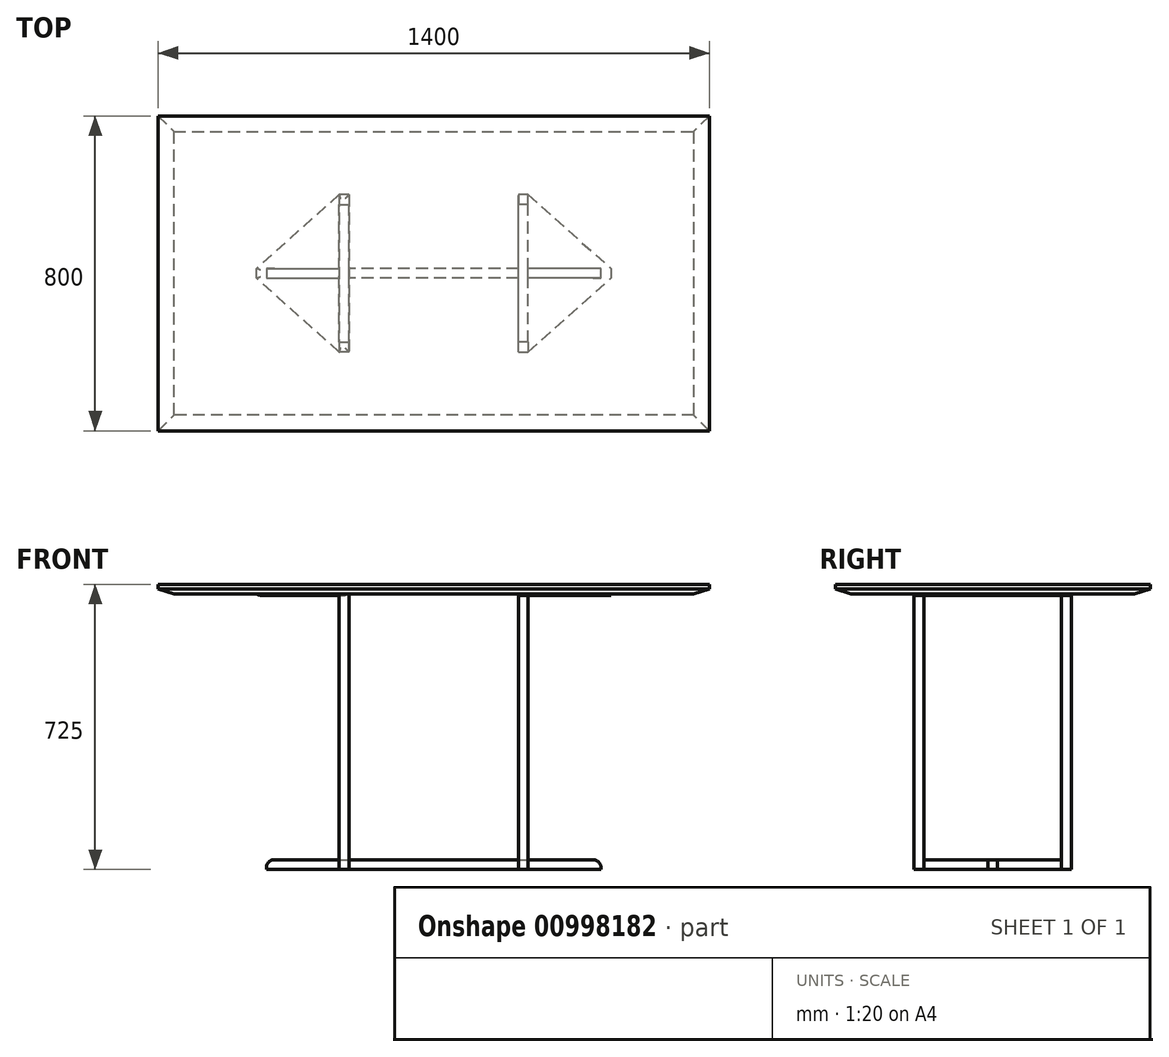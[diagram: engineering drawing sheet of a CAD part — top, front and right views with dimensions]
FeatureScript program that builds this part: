
annotation { "Feature Type Name" : "Feature", "Feature Type Description" : "" }
export const myFeature = defineFeature(function(context is Context, id is Id, definition is map)
    precondition{}
    {
        {
            var Q0;
            Q0=qCreatedBy(makeId("Top.planeOp"),FACE);
            var sketch = newSketch(context, id + "F0", { "sketchPlane" : qUnion([Q0])});
            skLineSegment(sketch, "E0.bottom", {"start": v(0, 0) * mm, "end": v(-1400, 0) * mm, "construction": true});
            skLineSegment(sketch, "E0.top", {"start": v(0, 800) * mm, "end": v(-1400, 800) * mm, "construction": true});
            skLineSegment(sketch, "E0.left", {"start": v(0, 0) * mm, "end": v(0, 800) * mm, "construction": true});
            skLineSegment(sketch, "E0.right", {"start": v(-1400, 0) * mm, "end": v(-1400, 800) * mm, "construction": true});
            skLineSegment(sketch, "E1", {"start": v(-700, 0) * mm, "end": v(-700, 800) * mm, "construction": true});
            skLineSegment(sketch, "E2", {"start": v(-1400, 400) * mm, "end": v(0, 400) * mm, "construction": true});
            skLineSegment(sketch, "E3", {"start": v(0, 400) * mm, "end": v(-250, 400) * mm, "construction": true});
            skLineSegment(sketch, "E4", {"start": v(0, 400) * mm, "end": v(-460, 400) * mm, "construction": true});
            skLineSegment(sketch, "E5", {"start": v(-460, 400) * mm, "end": v(-460, 800) * mm, "construction": true});
            skLineSegment(sketch, "E6", {"start": v(-460, 800) * mm, "end": v(-460, 600) * mm, "construction": true});
            skLineSegment(sketch, "E7", {"start": v(-460, 600) * mm, "end": v(-485, 600) * mm});
            skLineSegment(sketch, "E8", {"start": v(-485, 600) * mm, "end": v(-485, 575) * mm});
            skLineSegment(sketch, "E9", {"start": v(-485, 575) * mm, "end": v(-460, 575) * mm});
            skLineSegment(sketch, "E10", {"start": v(-460, 575) * mm, "end": v(-460, 600) * mm});
            skLineSegment(sketch, "E11.MirrorCS", {"start": v(-460, 200) * mm, "end": v(-485, 200) * mm});
            skLineSegment(sketch, "E12.MirrorCS", {"start": v(-485, 225) * mm, "end": v(-460, 225) * mm});
            skLineSegment(sketch, "E13.MirrorCS", {"start": v(-485, 200) * mm, "end": v(-485, 225) * mm});
            skLineSegment(sketch, "E14.MirrorCS", {"start": v(-460, 225) * mm, "end": v(-460, 200) * mm});
            skLineSegment(sketch, "E15.MirrorCS", {"start": v(-940, 600) * mm, "end": v(-915, 600) * mm});
            skLineSegment(sketch, "E16.MirrorCS", {"start": v(-915, 600) * mm, "end": v(-915, 575) * mm});
            skLineSegment(sketch, "E17.MirrorCS", {"start": v(-915, 575) * mm, "end": v(-940, 575) * mm});
            skLineSegment(sketch, "E18.MirrorCS", {"start": v(-915, 200) * mm, "end": v(-915, 225) * mm});
            skLineSegment(sketch, "E19.MirrorCS", {"start": v(-915, 225) * mm, "end": v(-940, 225) * mm});
            skLineSegment(sketch, "E20.MirrorCS", {"start": v(-940, 200) * mm, "end": v(-915, 200) * mm});
            skLineSegment(sketch, "E21.MirrorCS", {"start": v(-940, 225) * mm, "end": v(-940, 200) * mm});
            skLineSegment(sketch, "E22", {"start": v(-940, 600) * mm, "end": v(-940, 575) * mm});
            skSolve(sketch);
        }
        {
            var Q0;
            Q0=qSketchRegion(id+"F0",true);
            extrude(context, id + "F1", {"entities" : qUnion([Q0]), "depth" : 700 * mm, "offsetDistance" : 25 * mm});
        }
        {
            var Q0;
            Q0=makeQuery(id+"F1.opExtrude","SWEPT_FACE",FACE,{"disambiguationData":[OSD([sQuery(id+"F0.wireOp",EDGE,"E9")])]});
            cPlane(context, id + "F2", {"entities" : qUnion([Q0]), "cplaneType" : CPlaneType.OFFSET, "offset" : 0 * mm, "width" : 150 * mm, "height" : 150 * mm});
        }
        {
            var Q0;
            Q0=qCreatedBy(id+"F2.planeOp",FACE);
            var sketch = newSketch(context, id + "F3", { "sketchPlane" : qUnion([Q0])});
            skLineSegment(sketch, "E23", {"start": v(0, 0) * mm, "end": v(-460, 0) * mm});
            skLineSegment(sketch, "E24", {"start": v(-460, 0) * mm, "end": v(-485, 0) * mm});
            skLineSegment(sketch, "E25", {"start": v(-485, 0) * mm, "end": v(-485, 25) * mm});
            skLineSegment(sketch, "E26", {"start": v(-485, 25) * mm, "end": v(-460, 25) * mm});
            skLineSegment(sketch, "E27", {"start": v(-460, 25) * mm, "end": v(-460, 0) * mm});
            skSolve(sketch);
        }
        {
            var Q0;
            Q0=qSketchRegion(id+"F3",true);
            extrude(context, id + "F4", {"entities" : qUnion([Q0]), "depth" : 350 * mm, "offsetDistance" : 25 * mm});
        }
        {
            var Q0;
            Q0=makeQuery(id+"F4.opExtrude","SWEPT_FACE",FACE,{"disambiguationData":[OSD([sQuery(id+"F3.wireOp",EDGE,"E27")])]});
            cPlane(context, id + "F5", {"entities" : qUnion([Q0]), "cplaneType" : CPlaneType.OFFSET, "offset" : 0 * mm, "width" : 150 * mm, "height" : 150 * mm});
        }
        {
            var Q0;
            Q0=qCreatedBy(id+"F5.planeOp",FACE);
            var sketch = newSketch(context, id + "F6", { "sketchPlane" : qUnion([Q0])});
            skLineSegment(sketch, "E28", {"start": v(0, 0) * mm, "end": v(387.5, 0) * mm, "construction": true});
            skLineSegment(sketch, "E29", {"start": v(387.5, 0) * mm, "end": v(412.5, 0) * mm});
            skLineSegment(sketch, "E30", {"start": v(412.5, 0) * mm, "end": v(412.5, 25) * mm});
            skLineSegment(sketch, "E31", {"start": v(412.5, 25) * mm, "end": v(387.5, 25) * mm});
            skLineSegment(sketch, "E32", {"start": v(387.5, 25) * mm, "end": v(387.5, 0) * mm});
            skSolve(sketch);
        }
        {
            var Q0;
            Q0=qSketchRegion(id+"F6",true);
            extrude(context, id + "F7", {"entities" : qUnion([Q0]), "depth" : 185 * mm, "offsetDistance" : 25 * mm});
        }
        {
            var Q0;
            Q0=makeQuery(id+"F1.opExtrude","SWEPT_FACE",FACE,{"disambiguationData":[OSD([sQuery(id+"F0.wireOp",EDGE,"E17.MirrorCS")])]});
            cPlane(context, id + "F8", {"entities" : qUnion([Q0]), "cplaneType" : CPlaneType.OFFSET, "offset" : 0 * mm, "width" : 150 * mm, "height" : 150 * mm});
        }
        {
            var Q0;
            Q0=qCreatedBy(id+"F8.planeOp",FACE);
            var sketch = newSketch(context, id + "F9", { "sketchPlane" : qUnion([Q0])});
            skLineSegment(sketch, "E33", {"start": v(0, 0) * mm, "end": v(-700, 0) * mm, "construction": true});
            skLineSegment(sketch, "E34", {"start": v(-700, 0) * mm, "end": v(-915, 0) * mm, "construction": true});
            skLineSegment(sketch, "E35", {"start": v(-915, 0) * mm, "end": v(-940, 0) * mm});
            skLineSegment(sketch, "E36", {"start": v(-940, 0) * mm, "end": v(-940, 25) * mm});
            skLineSegment(sketch, "E37", {"start": v(-940, 25) * mm, "end": v(-915, 25) * mm});
            skLineSegment(sketch, "E38", {"start": v(-915, 25) * mm, "end": v(-915, 0) * mm});
            skSolve(sketch);
        }
        {
            var Q0;
            Q0=qSketchRegion(id+"F9",true);
            extrude(context, id + "F10", {"entities" : qUnion([Q0]), "operationType" : NewBodyOperationType.ADD, "depth" : 350 * mm, "offsetDistance" : 25 * mm});
        }
        {
            var Q0;
            Q0=makeQuery(id+"F10.boolean.opBoolean","MERGE",FACE,{"derivedFrom":[makeQuery(id+"F1.opExtrude","SWEPT_FACE",FACE,{"disambiguationData":[OSD([sQuery(id+"F0.wireOp",EDGE,"E22")])]}),makeQuery(id+"F10.opExtrude","SWEPT_FACE",FACE,{"disambiguationData":[OSD([sQuery(id+"F9.wireOp",EDGE,"E36")])]})]});
            cPlane(context, id + "F11", {"entities" : qUnion([Q0]), "cplaneType" : CPlaneType.OFFSET, "offset" : 0 * mm, "width" : 150 * mm, "height" : 150 * mm});
        }
        {
            var Q0;
            Q0=qCreatedBy(id+"F11.planeOp",FACE);
            var sketch = newSketch(context, id + "F12", { "sketchPlane" : qUnion([Q0])});
            skLineSegment(sketch, "E39", {"start": v(0, 0) * mm, "end": v(-387.5, 0) * mm, "construction": true});
            skLineSegment(sketch, "E40", {"start": v(-387.5, 0) * mm, "end": v(-387.5, 25) * mm});
            skLineSegment(sketch, "E41", {"start": v(-387.5, 25) * mm, "end": v(-412.5, 25) * mm});
            skLineSegment(sketch, "E42", {"start": v(-412.5, 25) * mm, "end": v(-412.5, 0) * mm});
            skLineSegment(sketch, "E43", {"start": v(-412.5, 0) * mm, "end": v(-387.5, 0) * mm});
            skSolve(sketch);
        }
        {
            var Q0;
            Q0=qSketchRegion(id+"F12",true);
            extrude(context, id + "F13", {"entities" : qUnion([Q0]), "depth" : 185 * mm, "offsetDistance" : 25 * mm});
        }
        {
            var Q0;
            Q0=makeQuery(id+"F1.opExtrude","CAP_FACE",FACE,{"disambiguationData":[OSD([sQuery(id+"F0.wireOp",EDGE,"E7"),sQuery(id+"F0.wireOp",EDGE,"E8"),sQuery(id+"F0.wireOp",EDGE,"E9"),sQuery(id+"F0.wireOp",EDGE,"E10")])],"isStart":false});
            cPlane(context, id + "F14", {"entities" : qUnion([Q0]), "cplaneType" : CPlaneType.OFFSET, "offset" : 0 * mm, "width" : 150 * mm, "height" : 150 * mm});
        }
        {
            var Q0;
            Q0=qCreatedBy(id+"F14.planeOp",FACE);
            var sketch = newSketch(context, id + "F15", { "sketchPlane" : qUnion([Q0])});
            skLineSegment(sketch, "E44.bottom", {"start": v(0, 0) * mm, "end": v(-1400, 0) * mm, "construction": true});
            skLineSegment(sketch, "E44.top", {"start": v(0, 800) * mm, "end": v(-1400, 800) * mm, "construction": true});
            skLineSegment(sketch, "E44.left", {"start": v(0, 0) * mm, "end": v(0, 800) * mm, "construction": true});
            skLineSegment(sketch, "E44.right", {"start": v(-1400, 0) * mm, "end": v(-1400, 800) * mm, "construction": true});
            skLineSegment(sketch, "E45", {"start": v(-700, 0) * mm, "end": v(-700, 400) * mm, "construction": true});
            skLineSegment(sketch, "E46", {"start": v(0, 400) * mm, "end": v(-250, 400) * mm, "construction": true});
            skLineSegment(sketch, "E47", {"start": v(-250, 400) * mm, "end": v(-250, 412.5) * mm});
            skLineSegment(sketch, "E48", {"start": v(-700, 400) * mm, "end": v(-485, 400) * mm, "construction": true});
            skLineSegment(sketch, "E49", {"start": v(-485, 400) * mm, "end": v(-485, 600) * mm});
            skLineSegment(sketch, "E50", {"start": v(-485, 600) * mm, "end": v(-460, 600) * mm});
            skLineSegment(sketch, "E51", {"start": v(-460, 600) * mm, "end": v(-250, 412.5) * mm});
            skLineSegment(sketch, "E52.MirrorCS", {"start": v(-460, 200) * mm, "end": v(-250, 387.5) * mm});
            skLineSegment(sketch, "E53.MirrorCS", {"start": v(-250, 400) * mm, "end": v(-250, 387.5) * mm});
            skLineSegment(sketch, "E54.MirrorCS", {"start": v(-485, 200) * mm, "end": v(-460, 200) * mm});
            skLineSegment(sketch, "E55.MirrorCS", {"start": v(-485, 400) * mm, "end": v(-485, 200) * mm});
            skLineSegment(sketch, "E56.MirrorCS", {"start": v(-940, 600) * mm, "end": v(-1150, 412.5) * mm});
            skLineSegment(sketch, "E57.MirrorCS", {"start": v(-1150, 400) * mm, "end": v(-1150, 412.5) * mm});
            skLineSegment(sketch, "E58.MirrorCS", {"start": v(-1150, 400) * mm, "end": v(-1150, 387.5) * mm});
            skLineSegment(sketch, "E59.MirrorCS", {"start": v(-940, 200) * mm, "end": v(-1150, 387.5) * mm});
            skLineSegment(sketch, "E60.MirrorCS", {"start": v(-915, 400) * mm, "end": v(-915, 600) * mm});
            skLineSegment(sketch, "E61.MirrorCS", {"start": v(-915, 400) * mm, "end": v(-915, 200) * mm});
            skLineSegment(sketch, "E62.MirrorCS", {"start": v(-915, 200) * mm, "end": v(-940, 200) * mm});
            skLineSegment(sketch, "E63.MirrorCS", {"start": v(-915, 600) * mm, "end": v(-940, 600) * mm});
            skSolve(sketch);
        }
        {
            var Q0;
            Q0=qSketchRegion(id+"F15",true);
            extrude(context, id + "F16", {"entities" : qUnion([Q0]), "oppositeDirection" : true, "depth" : 3 * mm, "offsetDistance" : 25 * mm});
        }
        {
            var Q0;
            Q0=makeQuery(id+"F16.opExtrude","CAP_FACE",FACE,{"disambiguationData":[OSD([sQuery(id+"F15.wireOp",EDGE,"E56.MirrorCS"),sQuery(id+"F15.wireOp",EDGE,"E57.MirrorCS"),sQuery(id+"F15.wireOp",EDGE,"E58.MirrorCS"),sQuery(id+"F15.wireOp",EDGE,"E59.MirrorCS"),sQuery(id+"F15.wireOp",EDGE,"E60.MirrorCS"),sQuery(id+"F15.wireOp",EDGE,"E61.MirrorCS"),sQuery(id+"F15.wireOp",EDGE,"E62.MirrorCS"),sQuery(id+"F15.wireOp",EDGE,"E63.MirrorCS")])],"isStart":true});
            cPlane(context, id + "F17", {"entities" : qUnion([Q0]), "cplaneType" : CPlaneType.OFFSET, "offset" : 0 * mm, "width" : 150 * mm, "height" : 150 * mm});
        }
        {
            var Q0;
            Q0=qCreatedBy(id+"F17.planeOp",FACE);
            var sketch = newSketch(context, id + "F18", { "sketchPlane" : qUnion([Q0])});
            skLineSegment(sketch, "E64.bottom", {"start": v(0, 0) * mm, "end": v(-1400, 0) * mm});
            skLineSegment(sketch, "E64.top", {"start": v(0, 800) * mm, "end": v(-1400, 800) * mm});
            skLineSegment(sketch, "E64.left", {"start": v(0, 0) * mm, "end": v(0, 800) * mm});
            skLineSegment(sketch, "E64.right", {"start": v(-1400, 0) * mm, "end": v(-1400, 800) * mm});
            skSolve(sketch);
        }
        {
            var Q0;
            Q0=qSketchRegion(id+"F18",true);
            extrude(context, id + "F19", {"entities" : qUnion([Q0]), "depth" : 25 * mm, "offsetDistance" : 25 * mm});
        }
        {
            var Q0;
            Q0=makeQuery(id+"F19.opExtrude","CAP_FACE",FACE,{"disambiguationData":[OSD([sQuery(id+"F18.wireOp",EDGE,"E64.bottom"),sQuery(id+"F18.wireOp",EDGE,"E64.top"),sQuery(id+"F18.wireOp",EDGE,"E64.left"),sQuery(id+"F18.wireOp",EDGE,"E64.right")])],"isStart":true});
            chamfer(context, id + "F20", {"entities" : qUnion([Q0]), "chamferType" : ChamferType.TWO_OFFSETS, "width1" : 40 * mm, "oppositeDirection" : false, "width2" : 12.5 * mm, "tangentPropagation" : true});
        }
        {
            var Q0;
            Q0=makeQuery(id+"F10.boolean.opBoolean","MERGE",FACE,{"derivedFrom":[makeQuery(id+"F1.opExtrude","SWEPT_FACE",FACE,{"disambiguationData":[OSD([sQuery(id+"F0.wireOp",EDGE,"E16.MirrorCS")])]}),makeQuery(id+"F10.opExtrude","SWEPT_FACE",FACE,{"disambiguationData":[OSD([sQuery(id+"F9.wireOp",EDGE,"E38")])]})]});
            cPlane(context, id + "F21", {"entities" : qUnion([Q0]), "cplaneType" : CPlaneType.OFFSET, "offset" : 0 * mm, "width" : 150 * mm, "height" : 150 * mm});
        }
        {
            var Q0;
            Q0=qCreatedBy(id+"F21.planeOp",FACE);
            var sketch = newSketch(context, id + "F22", { "sketchPlane" : qUnion([Q0])});
            skLineSegment(sketch, "E65", {"start": v(0, 0) * mm, "end": v(387.5, 0) * mm, "construction": true});
            skLineSegment(sketch, "E66.bottom", {"start": v(387.5, 0) * mm, "end": v(412.5, 0) * mm});
            skLineSegment(sketch, "E66.top", {"start": v(387.5, 25) * mm, "end": v(412.5, 25) * mm});
            skLineSegment(sketch, "E66.left", {"start": v(387.5, 0) * mm, "end": v(387.5, 25) * mm});
            skLineSegment(sketch, "E66.right", {"start": v(412.5, 0) * mm, "end": v(412.5, 25) * mm});
            skSolve(sketch);
        }
        {
            var Q0;
            Q0 = qSketchRegion(id + "F22", true);
            extrude(context, id + "F23", {"entities" : qUnion([Q0]), "depth" : 430 * mm, "offsetDistance" : 25 * mm});
        }
        {
            var Q0;
            Q0=makeQuery(id+"F16.opExtrude","CAP_FACE",FACE,{"disambiguationData":[OSD([sQuery(id+"F15.wireOp",EDGE,"E56.MirrorCS"),sQuery(id+"F15.wireOp",EDGE,"E57.MirrorCS"),sQuery(id+"F15.wireOp",EDGE,"E58.MirrorCS"),sQuery(id+"F15.wireOp",EDGE,"E59.MirrorCS"),sQuery(id+"F15.wireOp",EDGE,"E60.MirrorCS"),sQuery(id+"F15.wireOp",EDGE,"E61.MirrorCS"),sQuery(id+"F15.wireOp",EDGE,"E62.MirrorCS"),sQuery(id+"F15.wireOp",EDGE,"E63.MirrorCS")])],"isStart":false});
            var Q1;
            Q1=makeQuery(id+"F7.opExtrude","CAP_EDGE",EDGE,{"disambiguationData":[OSD([sQuery(id+"F6.wireOp",EDGE,"E31")])],"isStart":false});
            var Q2;
            Q2=makeQuery(id+"F13.opExtrude","CAP_EDGE",EDGE,{"disambiguationData":[OSD([sQuery(id+"F12.wireOp",EDGE,"E41")])],"isStart":false});
            fillet(context, id + "F24", {"entities" : qUnion([Q0, Q1, Q2]), "radius" : 20 * mm, "tangentPropagation" : true, "allowEdgeOverflow" : false});
        }
    });
